# Revit family: Furniture_GroheLimited_EssentialsToiletPaperHolder_40367000_METRICa
name_source: partatom
category: Furniture
revit_build: Autodesk Revit 2015 (Build: 20160512_0715(x64)
units: mm (PartAtom-declared; Revit-internal decimal feet)

## types (9) — shared parameters
ADACompliant = No
Assembly Code = C1030220
AssetType = Fixed
BIMObjectName = Furniture_GroheLimited_EssentialsToiletPaperHolder_40367000_METRIC
ClassificationName = Uniclass2015
ClassificationValue = Pr_40_20_76_88
Description = Essentials - Toilet paper holder with cover
DurationUnit = Years
Ecojoy = No
Features = Essentials - Toilet paper holder with cover
Height = 68 mm
IfcExportAs = IfcPipeFitting
IfcExportType = IfcPipeFittingType
Keynote = N13
Length = 167 mm  [stored 0.5479 ft]
LowEmittingMaterial = No
Manufacturer = Grohe Limited
ManufacturerName = Grohe Limited
MasterformatNumber = 22 41 39
MasterformatTitle = Residential Faucets, Supplies, and Trim
Model = Essentials Toilet paper holder
ModelReference = Essentials Toilet paper holder
NBSDescription = Toilet roll holders
NBSObjectName = Grohe Limited - Toilet roll holders
NBSReference = 45-35-72/368
NominalDepth = 121 mm  [stored 0.396982 ft]
NominalHeight = 68 mm
NominalLength = 167 mm  [stored 0.5479 ft]
ProductDocumentationLink = http://www.grohe.com
ProductPageURL = http://www.grohe.com
ProductionYear = 2017
ToiletPaper = Grohe-Toilet Paper
TypeName = Essentials Toilet paper holder
URL = www.grohe.com
WarrantyDurationUnit = Years
Width = 121 mm  [stored 0.396982 ft]
_BSBibleVersion = 14
_CurrentRevision = 1
_DistributedBy = www.bimstore.co.uk
zero-valued in all types: Cost, Default Elevation, ExpectedLife, _BimSpecGuid

## per-type parameters (varying)
| type | Color | Finish | Material | PrimaryMaterial |
| 40367000 | Chrome | Chrome | Chrome | GroheLimited-Chorme |
| 40367A01 | Hard Graphite | Hard Graphite | Hard Graphite | GroheLimited-HardGraphite |
| 40367AL1 | Brushed Hard Graphite | Brushed Hard Graphite | Brushed Hard Graphite | GroheLimited-BrushedHardGraphite |
| 40367BE1 | Nickel | Nickel | Nickel | GroheLimited-Nickel |
| 40367DA1 | Warm Sunset | Warm Sunset | Warm Sunset | GroheLimited-WarmSunset |
| 40367DL1 | Brushed Warm Sunset | Brushed Warm Sunset | Brushed Warm Sunset | GroheLimited-BrushedWarmSunset |
| 40367EN1 | Brushed Nickel | Brushed Nickel | Brushed Nickel | GroheLimited-BrushedNickel |
| 40367GL1 | Cool Sunrise | Cool Sunrise | Cool Sunrise | GroheLimited-CoolSunrise |
| 40367GN1 | Brushed Cool Sunrise | Brushed Cool Sunrise | Brushed Cool Sunrise | GroheLimited-BrushedCoolSunrise |

note: column(s) folded — value = type name in every type: ModelNumber, Type Comments

note: [stored X ft] marks values corroborated as IEEE doubles in the binary element streams (Revit-internal decimal feet)

## geometry (parser evidence)
native form markers: Blend x2, Sweep x3
no freeform markers — native parametric forms only
